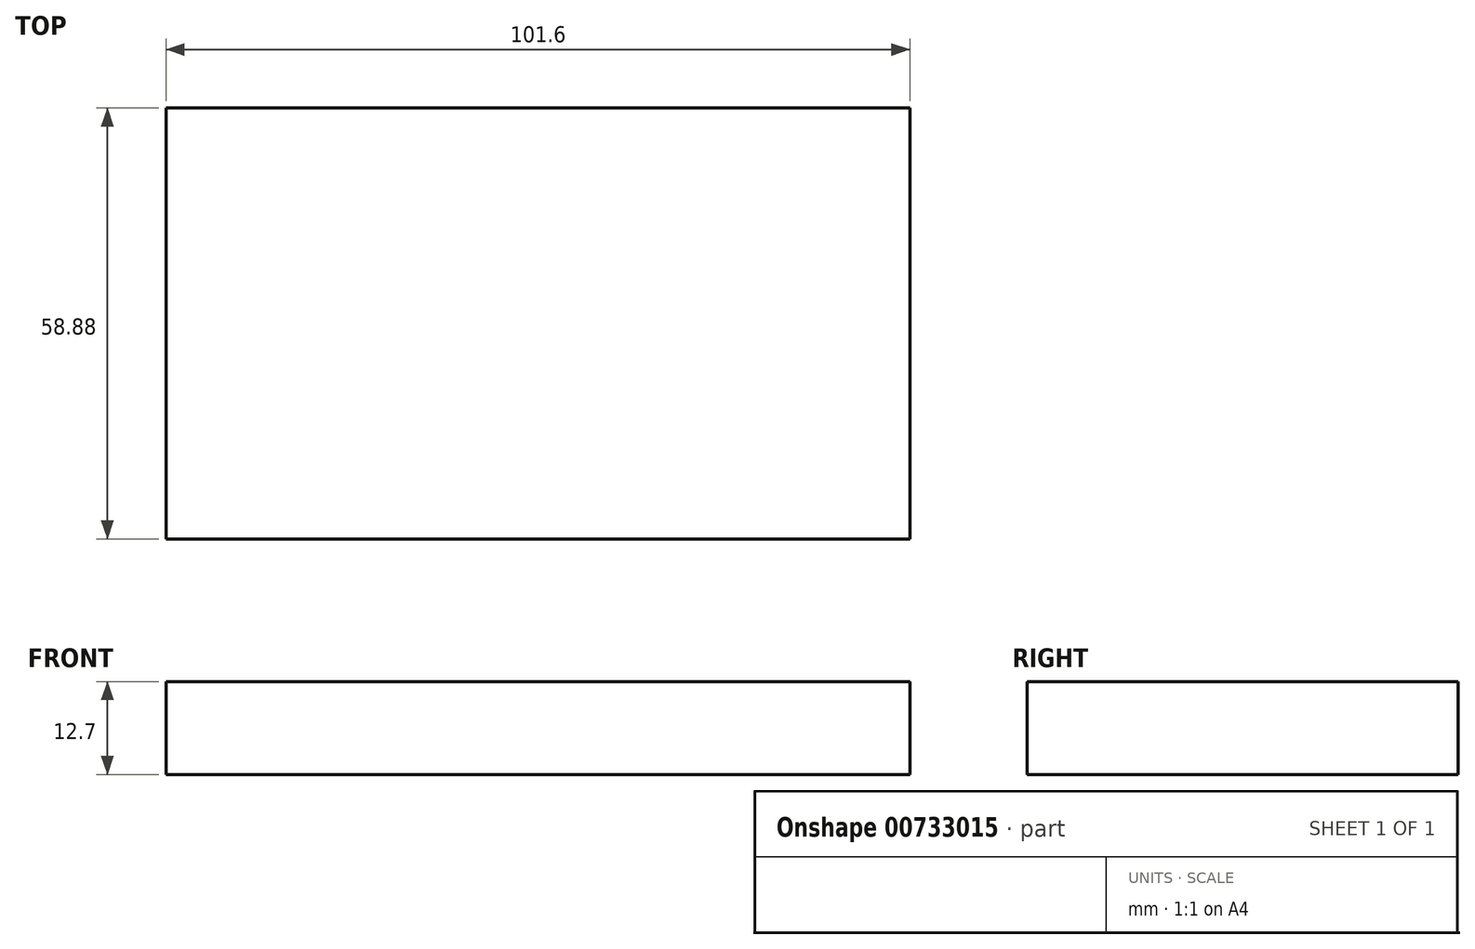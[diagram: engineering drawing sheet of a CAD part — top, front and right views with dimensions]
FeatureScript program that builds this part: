
annotation { "Feature Type Name" : "Feature", "Feature Type Description" : "" }
export const myFeature = defineFeature(function(context is Context, id is Id, definition is map)
    precondition{}
    {
        {
            var Q0;
            Q0=qCreatedBy(makeId("Right.planeOp"),FACE);
            var sketch = newSketch(context, id + "F0", { "sketchPlane" : qUnion([Q0])});
            skLineSegment(sketch, "E0", {"start": v(-31.6, 20.72) * mm, "end": v(27.27, 20.72) * mm});
            skLineSegment(sketch, "E1", {"start": v(-31.6, 20.72) * mm, "end": v(-31.6, 8.02) * mm});
            skLineSegment(sketch, "E2", {"start": v(27.27, 20.72) * mm, "end": v(27.27, 8.02) * mm});
            skLineSegment(sketch, "E3", {"start": v(27.27, 8.02) * mm, "end": v(-31.6, 8.02) * mm});
            skSolve(sketch);
        }
        {
            var Q0;
            Q0=makeQuery(id+"F0.imprint","IMPRINT",FACE,{"disambiguationData":[TD([[makeQuery(id+"F0.imprint","IMPRINT",EDGE,{"derivedFrom":sQuery(id+"F0.wireOp",EDGE,"E0")}),-1.0]])]});
            extrude(context, id + "F1", {"entities" : qUnion([Q0]), "endBound" : BoundingType.SYMMETRIC, "depth" : 101.6 * mm, "offsetDistance" : 25.4 * mm});
        }
    });
